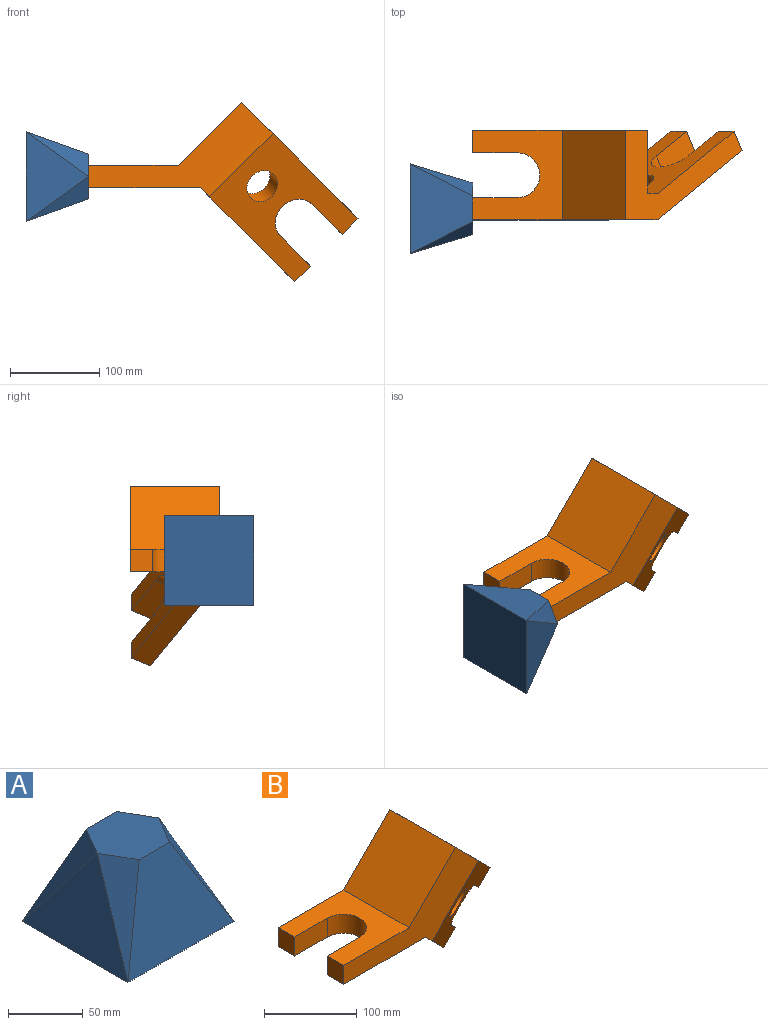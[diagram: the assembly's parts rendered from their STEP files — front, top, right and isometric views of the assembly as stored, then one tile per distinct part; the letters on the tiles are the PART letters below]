
ASSEMBLY  parts=2 mates=1
PART A: 10 faces, bbox 100x100x70 mm
  f0: plane 57.74x50mm, normal (0,0,1), area 2165.1mm2, adj f1,f4,f6,f7,f8,f9
  f1: plane 100x70mm, normal (0,0.94,0.34), area 4789.4mm2, adj f0,f5,f8,f9
  f2: plane 100x70mm, normal (-0.96,0,0.29), area 3656mm2, adj f5,f7,f8
  f3: plane 100x70mm, normal (0.96,0,0.29), area 3656mm2, adj f5,f6,f9
  f4: plane 100x70mm, normal (0,-0.94,0.34), area 4789.4mm2, adj f0,f5,f6,f7
  f5: plane 100x100mm, normal (0,0,-1), area 10000mm2, adj f1,f2,f3,f4
  f6: plane 70x50mm, normal (0.74,-0.43,0.53), area 1188mm2, adj f0,f3,f4
  f7: plane 70x50mm, normal (-0.74,-0.43,0.53), area 1188mm2, adj f0,f2,f4
  f8: plane 70x50mm, normal (-0.74,0.43,0.53), area 1188mm2, adj f0,f1,f2
  f9: plane 70x50mm, normal (0.74,0.43,0.53), area 1188mm2, adj f0,f1,f3
PART B: 22 faces, bbox 301x100x201 mm
  f0: plane 26.52x26.52mm, normal (0.61,0.5,-0.61), area 625mm2, adj f1,f11,f13,f20
  f1: plane 165.63x165.63mm, normal (0.35,-0.87,-0.35), area 10693mm2, adj f0,f5,f9,f11,f14,f18,f19,f20
  f2: plane 25x25mm, normal (-1,0,0), area 625mm2, adj f3,f7,f9,f16
  f3: plane 125x100mm, normal (0,0,-1), area 9018.3mm2, adj f2,f4,f8,f9,f10,f11,f15,f16
  f4: plane 70.71x70.71mm, normal (0.71,0,-0.71), area 7000mm2, adj f3,f5,f10,f12
  f5: plane 130.27x130.27mm, normal (0.71,0,0.71), area 7670.6mm2, adj f1,f4,f6,f9,f10,f12,f13,f14
  f6: plane 100x70.71mm, normal (-0.71,0,0.71), area 10000mm2, adj f5,f7,f9,f10
  f7: plane 100x100mm, normal (0,0,1), area 6518.3mm2, adj f2,f6,f8,f9,f10,f15,f16,f17
  f8: plane 25x25mm, normal (-1,0,0), area 625mm2, adj f3,f7,f10,f17
  f9: plane 206.07x106.07mm, normal (0,-1,0), area 7812.5mm2, adj f1,f2,f3,f5,f6,f7,f11
  f10: plane 195.71x95.71mm, normal (0,1,0), area 6348mm2, adj f3,f4,f5,f6,f7,f8
  f11: plane 105.27x105.27mm, normal (-0.71,0,-0.71), area 4135mm2, adj f0,f1,f3,f9,f12,f13
  f12: plane 82.45x82.45mm, normal (0,1,0), area 1660.6mm2, adj f4,f5,f11,f13
  f13: plane 155.4x155.4mm, normal (-0.35,0.87,0.35), area 9023.2mm2, adj f0,f5,f11,f12,f14,f18,f19,f20
  f14: plane 26.52x26.52mm, normal (0.61,0.5,-0.61), area 625mm2, adj f1,f5,f13,f18
  f15: cylinder r=25mm len=50mm, axis (0,0,-1), area 1963.5mm2, adj f3,f7,f16,f17
  f16: plane 50x25mm, normal (0,1,0), area 1250mm2, adj f2,f3,f7,f15
  f17: plane 50x25mm, normal (0,-1,0), area 1250mm2, adj f3,f7,f8,f15
  f18: plane 49.15x42.52mm, normal (-0.71,0,-0.71), area 1375mm2, adj f1,f13,f14,f19
  f19: cylinder r=25mm len=49.9mm, axis (0.35,-0.87,-0.35), area 1963.5mm2, adj f1,f13,f18,f20
  f20: plane 49.15x42.52mm, normal (0.71,0,0.71), area 1375mm2, adj f0,f1,f13,f19
  f21: cylinder r=18.5mm len=43.45mm, axis (0.35,-0.87,-0.35), area 2906mm2, adj f1,f13
PLACE A rot(axis=(-0.58,0.58,-0.58),120deg) t=(-195,-37.5,12.5)mm
PLACE B at identity
MATE fastened A.f0 <-> B.f2  axis (1,0,0) through (-125,-37.5,12.5)mm
